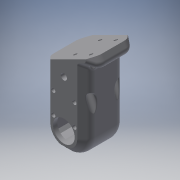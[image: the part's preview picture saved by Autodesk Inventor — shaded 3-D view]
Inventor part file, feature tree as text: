
AUTODESK INVENTOR PART (.ipt)
format: ipt  version: 2018 (Build 220112000, 112)  size: 1,025,024 bytes
history: native  units: mm
features: sketch x30, projected_geometry x26, extrude x23, hole x10, fillet x10, chamfer x3, mirror x1, plane x1
ambient origin geometry x8: Origin, YZ Plane, XZ Plane, XY Plane, X Axis, Y Axis, Z Axis, Center Point
bodies: Solid1 (feature_tree)
feature tree (104):
  extrude  "Extrusion1"  Depth=45.0mm
  extrude  "Extrusion2"  Depth=2.25mm
  hole  "Hole1"  [1 undecoded]
  hole  "Hole2"  [1 undecoded]
  fillet  "Fillet1"  Radius=14.0mm
  extrude  "Extrusion3"  Depth=18.5mm
  extrude  "Extrusion4"  Depth=10.0mm
  extrude  "Extrusion5"  Depth=2.0mm
  extrude  "Extrusion6"  Depth=2.0mm
  hole  "Hole3"  [1 undecoded]
  extrude  "Extrusion7"  Depth=0.5mm
  extrude  "Extrusion8"  Depth=5.0mm TaperAngle=0.0deg
  extrude  "Extrusion9"  Depth=10.0mm
  extrude  "Extrusion10"  Depth=10.0mm
  extrude  "Extrusion11"  Depth=14.5mm
  extrude  "Extrusion12"  Depth=20.0mm
  extrude  "Extrusion13"  Depth=5.0mm
  extrude  "Extrusion14"  Depth=2.25mm
  extrude  "Extrusion15"  Depth=5.0mm
  extrude  "Extrusion16"  Depth=9.0mm
  extrude  "Extrusion17"  Depth=1.0mm
  chamfer  "Chamfer1"  Distance=1.0mm
  fillet  "Fillet7"  Radius=20.7mm
  fillet  "Fillet8"  Radius=32.0mm
  mirror  "Mirror1"
  extrude  "Extrusion24"  Depth=1.0mm TaperAngle=0.0deg
  extrude  "Extrusion25"  Depth=8.0mm
  extrude  "Extrusion26"  Depth=0.2mm TaperAngle=0.0deg
  extrude  "Extrusion27"  Depth=0.5mm TaperAngle=0.0deg
  extrude  "Extrusion28"  Depth=5.0mm TaperAngle=0.0deg
  chamfer  "Chamfer5"  Distance=5.0mm
  fillet  "Fillet18"  Radius=0.2mm
  fillet  "Fillet19"  Radius=0.2mm
  extrude  "Extrusion29"  Depth=2.0mm
  chamfer  "Chamfer6"  Distance=40.0mm
  hole  "Hole10"  [1 undecoded]
  plane  "Work Plane2"
  hole  "Hole11"  [1 undecoded]
  fillet  "Fillet20"  Radius=10.0mm
  sketch  "Sketch43"  dims[d102=2.5mm d103=2.0mm d104=45.0deg d105=1.5mm]
  hole  "Hole12"  [1 undecoded]
  hole  "Hole13"  [1 undecoded]
  hole  "Hole14"  [1 undecoded]
  fillet  "Fillet21"  Radius=8.0mm
  fillet  "Fillet22"  Radius=10.0mm
  hole  "Hole15"  [1 undecoded]
  fillet  "Fillet23"  Radius=2.0mm
  hole  "Hole16"  [1 undecoded]
  fillet  "Fillet24"  Radius=8.0mm
  sketch  "Sketch1"  dims[d0=24.5mm d1=45.0mm]
  sketch  "Sketch2"  dims[d2=1.95mm d3=0.0mm d4=2.25mm]
  projected_geometry  "Projected Loop1"
  sketch  "Sketch3"  dims[d5=20.0mm d6=2.25mm]
  projected_geometry  "Projected Loop2"
  sketch  "Sketch4"  dims[d7=5.25mm d8=5.25mm d9=14.0mm]
  projected_geometry  "Projected Loop3"
  sketch  "Sketch5"  dims[d10=5.25mm d11=18.5mm]
  projected_geometry  "Projected Loop4"
  sketch  "Sketch6"  dims[d12=10.0mm d13=0.0mm d14=20.5mm]
  projected_geometry  "Projected Loop5"
  sketch  "Sketch7"  dims[d15=2.0mm d16=2.195mm]
  projected_geometry  "Projected Loop6"
  sketch  "Sketch8"  dims[d17=2.0mm]
  projected_geometry  "Projected Loop7"
  sketch  "Sketch9"  dims[d18=2.4mm d19=6.0mm d20=4.4mm d21=2.0mm d22=90.0deg d23=8.0mm d24=20.594885mm d25=20.5mm]
  projected_geometry  "Projected Loop8"
  projected_geometry  "Projected Loop9"
  sketch  "Sketch10"  dims[d26=26.65mm d27=2.0mm]
  projected_geometry  "Projected Loop10"
  projected_geometry  "Projected Loop11"
  sketch  "Sketch11"  dims[d28=2.0mm]
  projected_geometry  "Projected Loop12"
  sketch  "Sketch12"  dims[d29=2.4mm d30=6.0mm d31=4.4mm d32=2.0mm d33=90.0deg d34=8.0mm d35=20.594885mm d36=0.5mm]
  sketch  "Sketch13"  dims[d37=18.0mm d38=5.0mm d39=0.0mm]
  sketch  "Sketch14"  dims[d41=10.0mm d42=0.0mm d43=24.5mm]
  projected_geometry  "Projected Loop13"
  sketch  "Sketch15"  dims[d44=1.15mm d45=0.0mm d46=10.0mm]
  sketch  "Sketch16"  dims[d47=21.0mm d48=14.5mm]
  projected_geometry  "Projected Loop14"
  sketch  "Sketch17"  dims[d49=20.0mm d50=14.5mm]
  projected_geometry  "Projected Loop15"
  sketch  "Sketch18"  dims[d51=24.5mm d52=5.0mm]
  projected_geometry  "Projected Loop16"
  sketch  "Sketch19"  dims[d53=5.0mm d54=2.25mm]
  projected_geometry  "Projected Loop17"
  sketch  "Sketch20"  dims[d55=2.25mm d56=5.0mm]
  projected_geometry  "Projected Loop18"
  sketch  "Sketch35"  dims[d57=5.0mm d58=9.0mm]
  projected_geometry  "Projected Loop28"
  sketch  "Sketch36"  dims[d59=14.75mm d60=4.0mm d61=1.0mm d62=0.0mm d63=20.7mm]
  projected_geometry  "Projected Loop29"
  sketch  "Sketch37"  dims[d64=2.4mm d65=6.0mm d66=4.4mm d67=2.0mm d68=90.0deg d69=8.0mm d70=20.594885mm d72=32.0mm]
  sketch  "Sketch38"  dims[d73=5.0mm d74=0.0mm d75=1.0mm d76=0.0mm]
  sketch  "Sketch39"  dims[d77=12.25mm d78=0.0mm d80=8.0mm]
  projected_geometry  "Projected Loop30"
  sketch  "Sketch40"  dims[d81=4.5mm d82=0.0mm d84=0.2mm d85=0.0mm]
  projected_geometry  "Projected Loop31"
  sketch  "Sketch41"  dims[d86=21.0mm d87=0.5mm d88=0.0mm]
  projected_geometry  "Projected Loop32"
  projected_geometry  "Projected Loop33"
  sketch  "Sketch42"  dims[d91=8.0mm d92=0.0mm d93=5.0mm d94=0.0mm d95=5.0mm d96=0.0mm d98=0.2mm d99=0.0mm d100=0.2mm d101=0.0mm]
  projected_geometry  "Projected Loop34"
  sketch  "Sketch44"  dims[d114=0.5mm d187=40.0mm d188=70.0mm d189=20.0mm d190=10.0mm d191=0.0mm d192=10.0mm d193=0.0mm d194=2.0mm d195=0.0mm d196=2.0mm d197=0.0mm d198=8.0mm d199=10.0mm d200=2.0mm d201=0.0mm d204=7.0mm d205=2.0mm d206=45.0deg d207=5.0mm d208=8.0mm d209=15.0mm d210=2.0mm d211=0.0mm d212=1.5mm d213=2.0mm d214=45.0deg d215=24.0mm d216=17.0mm d217=3.5mm d218=3.2mm d219=6.0mm d220=9.4mm d221=2.0mm d222=90.0deg d223=8.0mm d224=20.594885mm d225=6.0mm d226=6.0mm d227=9.4mm d228=2.0mm d229=90.0deg d230=69.0mm d231=0.0mm d232=1.0mm d233=8.0mm d234=2.459mm d235=6.0mm d236=9.4mm d237=2.0mm d238=90.0deg d239=34.0mm d240=20.594885mm d241=3.2mm d242=6.0mm d243=6.3mm d244=2.0mm d245=90.0deg d246=20.55mm d247=0.0mm d248=6.0mm d249=6.0mm d250=6.3mm d251=2.0mm d252=90.0deg d253=10.0mm d254=0.0mm d255=1.5mm d256=0.75mm d257=4.0mm d258=6.0mm d259=4.4mm d260=2.0mm d261=90.0deg d262=2.5mm d263=0.0mm d264=1.0mm d265=4.0mm d266=6.0mm d267=4.4mm d268=2.0mm d269=90.0deg d270=2.5mm d271=0.0mm d272=1.0mm]
  projected_geometry  "Projected Loop35"
note: 10 required parameter values undecoded (feature->parameter linkage not recoverable at this tier; creation-order binding heuristic only, values carry confidence <= 0.55)
